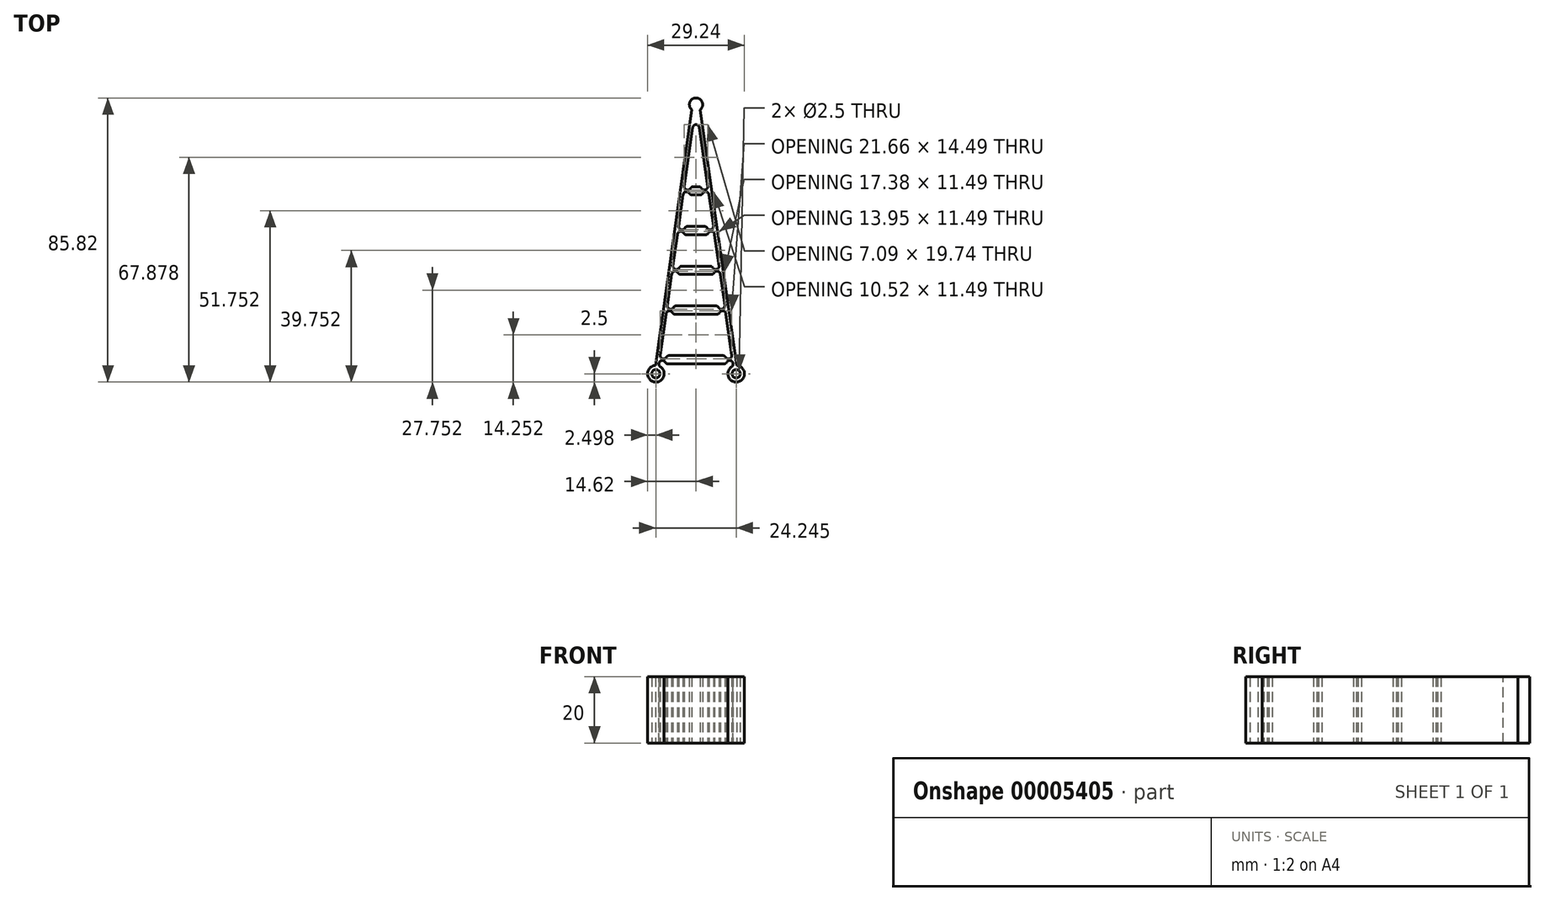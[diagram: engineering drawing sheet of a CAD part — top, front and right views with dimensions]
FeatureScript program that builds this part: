
annotation { "Feature Type Name" : "Feature", "Feature Type Description" : "" }
export const myFeature = defineFeature(function(context is Context, id is Id, definition is map)
    precondition{}
    {
        {
            var Q0;
            Q0=qCreatedBy(makeId("Top.planeOp"),FACE);
            var sketch = newSketch(context, id + "F0", { "sketchPlane" : qUnion([Q0])});
            skLineSegment(sketch, "E0", {"start": v(10, 0) * mm, "end": v(0, 70) * mm});
            skLineSegment(sketch, "E1", {"start": v(0, 70) * mm, "end": v(-10, 0) * mm});
            skLineSegment(sketch, "E2", {"start": v(-10, 0) * mm, "end": v(10, 0) * mm});
            skLineSegment(sketch, "E3", {"start": v(-2.71, 51) * mm, "end": v(2.71, 51) * mm});
            skLineSegment(sketch, "E4", {"start": v(-4.43, 39) * mm, "end": v(4.43, 39) * mm});
            skLineSegment(sketch, "E5", {"start": v(-6.14, 27) * mm, "end": v(6.14, 27) * mm});
            skLineSegment(sketch, "E6", {"start": v(-7.86, 15) * mm, "end": v(7.86, 15) * mm});
            skCircle(sketch, "E7", {"center": v(2.71, 51) * mm, "radius": 1.5 * mm});
            skCircle(sketch, "E8", {"center": v(4.43, 39) * mm, "radius": 1.5 * mm});
            skCircle(sketch, "E9", {"center": v(6.14, 27) * mm, "radius": 1.5 * mm});
            skCircle(sketch, "E10", {"center": v(7.86, 15) * mm, "radius": 1.5 * mm});
            skCircle(sketch, "E11", {"center": v(10, 0) * mm, "radius": 1.5 * mm});
            skSolve(sketch);
        }
        {
            var Q0;
            Q0=qCreatedBy(makeId("Top.planeOp"),FACE);
            var sketch = newSketch(context, id + "F1", { "sketchPlane" : qUnion([Q0])});
            skLineSegment(sketch, "E12", {"start": v(0, 77.07) * mm, "end": v(11.62, -4.25) * mm});
            skLineSegment(sketch, "E13", {"start": v(11.62, -4.25) * mm, "end": v(12.63, -4.25) * mm});
            skLineSegment(sketch, "E14", {"start": v(12.63, -4.25) * mm, "end": v(0.99, 77.21) * mm});
            skLineSegment(sketch, "E15", {"start": v(0.99, 77.21) * mm, "end": v(0, 77.07) * mm});
            skLineSegment(sketch, "E16", {"start": v(0, 77.07) * mm, "end": v(0, 0) * mm, "construction": true});
            skLineSegment(sketch, "E17.bottom", {"start": v(0, 49.75) * mm, "end": v(3.9, 49.75) * mm});
            skLineSegment(sketch, "E17.top", {"start": v(0, 52.25) * mm, "end": v(3.9, 52.25) * mm});
            skLineSegment(sketch, "E17.left", {"start": v(0, 49.75) * mm, "end": v(0, 52.25) * mm});
            skLineSegment(sketch, "E17.right", {"start": v(3.9, 49.75) * mm, "end": v(3.9, 52.25) * mm});
            skLineSegment(sketch, "E18.bottom", {"start": v(0, 40.25) * mm, "end": v(5.62, 40.25) * mm});
            skLineSegment(sketch, "E18.top", {"start": v(0, 37.75) * mm, "end": v(5.62, 37.75) * mm});
            skLineSegment(sketch, "E18.left", {"start": v(0, 40.25) * mm, "end": v(0, 37.75) * mm});
            skLineSegment(sketch, "E18.right", {"start": v(5.62, 40.25) * mm, "end": v(5.62, 37.75) * mm});
            skLineSegment(sketch, "E19.bottom", {"start": v(0, 28.25) * mm, "end": v(7.33, 28.25) * mm});
            skLineSegment(sketch, "E19.top", {"start": v(0, 25.75) * mm, "end": v(7.33, 25.75) * mm});
            skLineSegment(sketch, "E19.left", {"start": v(0, 28.25) * mm, "end": v(0, 25.75) * mm});
            skLineSegment(sketch, "E19.right", {"start": v(7.33, 28.25) * mm, "end": v(7.33, 25.75) * mm});
            skLineSegment(sketch, "E20.bottom", {"start": v(0, 16.25) * mm, "end": v(9.05, 16.25) * mm});
            skLineSegment(sketch, "E20.top", {"start": v(0, 13.75) * mm, "end": v(9.05, 13.75) * mm});
            skLineSegment(sketch, "E20.left", {"start": v(0, 16.25) * mm, "end": v(0, 13.75) * mm});
            skLineSegment(sketch, "E20.right", {"start": v(9.05, 16.25) * mm, "end": v(9.05, 13.75) * mm});
            skLineSegment(sketch, "E21.bottom", {"start": v(0, 1.25) * mm, "end": v(11.19, 1.25) * mm});
            skLineSegment(sketch, "E21.top", {"start": v(0, -1.25) * mm, "end": v(11.19, -1.25) * mm});
            skLineSegment(sketch, "E21.left", {"start": v(0, 1.25) * mm, "end": v(0, -1.25) * mm});
            skLineSegment(sketch, "E21.right", {"start": v(11.19, 1.25) * mm, "end": v(11.19, -1.25) * mm});
            skPoint(sketch, "E22", {"position": v(0, 51) * mm});
            skPoint(sketch, "E23", {"position": v(0, 39) * mm});
            skPoint(sketch, "E24", {"position": v(0, 27) * mm});
            skPoint(sketch, "E25", {"position": v(0, 15) * mm});
            skArc(sketch, "E26", {"start": v(0.28, 75.1) * mm, "mid": v(1.31, 78.58) * mm, "end": v(-2, 77.07) * mm});
            skLineSegment(sketch, "E27", {"start": v(0, 77.07) * mm, "end": v(-2, 77.07) * mm});
            skCircle(sketch, "E28", {"center": v(12.12, -4.25) * mm, "radius": 2.5 * mm});
            skSolve(sketch);
        }
        {
            var Q0;
            Q0=qCreatedBy(makeId("Top.planeOp"),FACE);
            var sketch = newSketch(context, id + "F2", { "sketchPlane" : qUnion([Q0])});
            skCircle(sketch, "E29", {"center": v(2.54, 52.25) * mm, "radius": 1 * mm});
            skCircle(sketch, "E30", {"center": v(2.9, 49.75) * mm, "radius": 1 * mm});
            skCircle(sketch, "E31", {"center": v(4.25, 40.25) * mm, "radius": 1 * mm});
            skCircle(sketch, "E32", {"center": v(4.6, 37.75) * mm, "radius": 1 * mm});
            skCircle(sketch, "E33", {"center": v(5.96, 28.25) * mm, "radius": 1 * mm});
            skCircle(sketch, "E34", {"center": v(6.32, 25.75) * mm, "radius": 1 * mm});
            skCircle(sketch, "E35", {"center": v(7.68, 16.25) * mm, "radius": 1 * mm});
            skCircle(sketch, "E36", {"center": v(8.04, 13.75) * mm, "radius": 1 * mm});
            skCircle(sketch, "E37", {"center": v(9.82, 1.25) * mm, "radius": 1 * mm});
            skCircle(sketch, "E38", {"center": v(10.18, -1.25) * mm, "radius": 1 * mm});
            skSolve(sketch);
        }
        {
            var Q0;
            Q0=qCreatedBy(makeId("Top.planeOp"),FACE);
            var sketch = newSketch(context, id + "F3", { "sketchPlane" : qUnion([Q0])});
            skCircle(sketch, "E39", {"center": v(12.12, -4.25) * mm, "radius": 1.25 * mm});
            skSolve(sketch);
        }
        {
            var Q0;
            {var subQ4=sQuery(id+"F1.wireOp",EDGE,"E17.bottom");var subQ5=sQuery(id+"F1.wireOp",EDGE,"E17.right");var subQ9=sQuery(id+"F1.wireOp",EDGE,"E18.top");var subQ12=sQuery(id+"F1.wireOp",EDGE,"E18.right");var subQ16=sQuery(id+"F1.wireOp",EDGE,"E19.top");var subQ19=sQuery(id+"F1.wireOp",EDGE,"E19.right");var subQ23=sQuery(id+"F1.wireOp",EDGE,"E20.top");var subQ26=sQuery(id+"F1.wireOp",EDGE,"E20.right");var subQ30=sQuery(id+"F1.wireOp",EDGE,"E21.top");var subQ33=sQuery(id+"F1.wireOp",EDGE,"E21.right");var subQ40=sQuery(id+"F1.wireOp",EDGE,"E13");var subQ42=makeQuery(id+"F1.imprint","IMPRINT",EDGE,{"derivedFrom":subQ40});var subQ47=sQuery(id+"F1.wireOp",EDGE,"E15");var subQ48=makeQuery(id+"F1.imprint","IMPRINT",EDGE,{"derivedFrom":subQ47});var subQ52=makeQuery(id+"F1.imprint","IMPRINT",EDGE,{"derivedFrom":subQ5});var subQ54=makeQuery(id+"F1.imprint","IMPRINT",EDGE,{"derivedFrom":subQ12});var subQ56=makeQuery(id+"F1.imprint","IMPRINT",EDGE,{"derivedFrom":subQ19});var subQ58=makeQuery(id+"F1.imprint","IMPRINT",EDGE,{"derivedFrom":subQ26});var subQ60=makeQuery(id+"F1.imprint","IMPRINT",EDGE,{"derivedFrom":subQ33});Q0=qUnion([makeQuery(id+"F1.imprint","IMPRINT",FACE,{"disambiguationData":[TD([[makeQuery(id+"F1.imprint","IMPRINT",EDGE,{"derivedFrom":subQ4}),1.0]])]}),makeQuery(id+"F1.imprint","IMPRINT",FACE,{"disambiguationData":[TD([[makeQuery(id+"F1.imprint","IMPRINT",EDGE,{"derivedFrom":subQ9}),1.0]])]}),makeQuery(id+"F1.imprint","IMPRINT",FACE,{"disambiguationData":[TD([[makeQuery(id+"F1.imprint","IMPRINT",EDGE,{"derivedFrom":subQ16}),1.0]])]}),makeQuery(id+"F1.imprint","IMPRINT",FACE,{"disambiguationData":[TD([[makeQuery(id+"F1.imprint","IMPRINT",EDGE,{"derivedFrom":subQ23}),1.0]])]}),makeQuery(id+"F1.imprint","IMPRINT",FACE,{"disambiguationData":[TD([[makeQuery(id+"F1.imprint","IMPRINT",EDGE,{"derivedFrom":subQ30}),1.0]])]}),makeQuery(id+"F1.imprint","IMPRINT",FACE,{"disambiguationData":[TD([[subQ42,-1.0]])]}),makeQuery(id+"F1.imprint","IMPRINT",FACE,{"disambiguationData":[TD([[subQ48,-1.0]])]}),makeQuery(id+"F1.imprint","IMPRINT",FACE,{"disambiguationData":[TD([[subQ48,1.0]])]}),makeQuery(id+"F1.imprint","IMPRINT",FACE,{"disambiguationData":[TD([[subQ52,1.0]])]}),makeQuery(id+"F1.imprint","IMPRINT",FACE,{"disambiguationData":[TD([[subQ54,-1.0]])]}),makeQuery(id+"F1.imprint","IMPRINT",FACE,{"disambiguationData":[TD([[subQ56,-1.0]])]}),makeQuery(id+"F1.imprint","IMPRINT",FACE,{"disambiguationData":[TD([[subQ58,-1.0]])]}),makeQuery(id+"F1.imprint","IMPRINT",FACE,{"disambiguationData":[TD([[subQ60,-1.0]])]}),makeQuery(id+"F1.imprint","IMPRINT",FACE,{"disambiguationData":[TD([[subQ42,1.0]])]}),makeQuery(id+"F1.imprint","IMPRINT",FACE,{"disambiguationData":[TD([[subQ52,-1.0]])]})]);}
            var Q1;
            {var subQ5=sQuery(id+"F1.wireOp",EDGE,"E13");Q1=makeQuery(id+"F1.imprint","IMPRINT",FACE,{"disambiguationData":[TD([[makeQuery(id+"F1.imprint","IMPRINT",EDGE,{"derivedFrom":subQ5}),1.0]])]});}
            extrude(context, id + "F4", {"entities" : qUnion([Q0, Q1]), "depth" : 20 * mm});
        }
        {
            var Q0;
            {Q0=qUnion([makeQuery(id+"F2.imprint","IMPRINT",FACE,{"disambiguationData":[TD([[makeQuery(id+"F2.imprint","IMPRINT",EDGE,{"derivedFrom":sQuery(id+"F2.wireOp",EDGE,"E29")}),1.0]])]}),makeQuery(id+"F2.imprint","IMPRINT",FACE,{"disambiguationData":[TD([[makeQuery(id+"F2.imprint","IMPRINT",EDGE,{"derivedFrom":sQuery(id+"F2.wireOp",EDGE,"E30")}),1.0]])]}),makeQuery(id+"F2.imprint","IMPRINT",FACE,{"disambiguationData":[TD([[makeQuery(id+"F2.imprint","IMPRINT",EDGE,{"derivedFrom":sQuery(id+"F2.wireOp",EDGE,"E31")}),1.0]])]}),makeQuery(id+"F2.imprint","IMPRINT",FACE,{"disambiguationData":[TD([[makeQuery(id+"F2.imprint","IMPRINT",EDGE,{"derivedFrom":sQuery(id+"F2.wireOp",EDGE,"E32")}),1.0]])]}),makeQuery(id+"F2.imprint","IMPRINT",FACE,{"disambiguationData":[TD([[makeQuery(id+"F2.imprint","IMPRINT",EDGE,{"derivedFrom":sQuery(id+"F2.wireOp",EDGE,"E33")}),1.0]])]}),makeQuery(id+"F2.imprint","IMPRINT",FACE,{"disambiguationData":[TD([[makeQuery(id+"F2.imprint","IMPRINT",EDGE,{"derivedFrom":sQuery(id+"F2.wireOp",EDGE,"E34")}),1.0]])]}),makeQuery(id+"F2.imprint","IMPRINT",FACE,{"disambiguationData":[TD([[makeQuery(id+"F2.imprint","IMPRINT",EDGE,{"derivedFrom":sQuery(id+"F2.wireOp",EDGE,"E35")}),1.0]])]}),makeQuery(id+"F2.imprint","IMPRINT",FACE,{"disambiguationData":[TD([[makeQuery(id+"F2.imprint","IMPRINT",EDGE,{"derivedFrom":sQuery(id+"F2.wireOp",EDGE,"E36")}),1.0]])]}),makeQuery(id+"F2.imprint","IMPRINT",FACE,{"disambiguationData":[TD([[makeQuery(id+"F2.imprint","IMPRINT",EDGE,{"derivedFrom":sQuery(id+"F2.wireOp",EDGE,"E37")}),1.0]])]}),makeQuery(id+"F2.imprint","IMPRINT",FACE,{"disambiguationData":[TD([[makeQuery(id+"F2.imprint","IMPRINT",EDGE,{"derivedFrom":sQuery(id+"F2.wireOp",EDGE,"E38")}),1.0]])]})]);}
            extrude(context, id + "F5", {"entities" : qUnion([Q0]), "operationType" : NewBodyOperationType.REMOVE, "endBound" : BoundingType.THROUGH_ALL, "depth" : 25 * mm});
        }
        {
            var Q0;
            Q0=makeQuery(id+"F3.imprint","IMPRINT",FACE,{"disambiguationData":[TD([[makeQuery(id+"F3.imprint","IMPRINT",EDGE,{"derivedFrom":sQuery(id+"F3.wireOp",EDGE,"E39")}),1.0]])]});
            extrude(context, id + "F6", {"entities" : qUnion([Q0]), "operationType" : NewBodyOperationType.REMOVE, "endBound" : BoundingType.THROUGH_ALL, "depth" : 25 * mm});
        }
        {
            var Q0;
            Q0=makeQuery(id+"F5.boolean.opBoolean","INTERSECT",EDGE,{"disambiguationData":[OD(0.0)],"derivedFrom":[makeQuery(id+"F4.opExtrude","SWEPT_FACE",FACE,{"disambiguationData":[OSD([sQuery(id+"F1.wireOp",EDGE,"E17.top")])]}),makeQuery(id+"F5.opExtrude","SWEPT_FACE",FACE,{"disambiguationData":[OSD([sQuery(id+"F2.wireOp",EDGE,"E29")])]})]});
            var Q1;
            Q1=makeQuery(id+"F5.boolean.opBoolean","INTERSECT",EDGE,{"disambiguationData":[OD(0.0)],"derivedFrom":[makeQuery(id+"F4.opExtrude","SWEPT_FACE",FACE,{"disambiguationData":[OSD([sQuery(id+"F1.wireOp",EDGE,"E17.bottom")])]}),makeQuery(id+"F5.opExtrude","SWEPT_FACE",FACE,{"disambiguationData":[OSD([sQuery(id+"F2.wireOp",EDGE,"E30")])]})]});
            var Q2;
            Q2=makeQuery(id+"F5.boolean.opBoolean","INTERSECT",EDGE,{"disambiguationData":[OD(0.0)],"derivedFrom":[makeQuery(id+"F4.opExtrude","SWEPT_FACE",FACE,{"disambiguationData":[OSD([sQuery(id+"F1.wireOp",EDGE,"E18.bottom")])]}),makeQuery(id+"F5.opExtrude","SWEPT_FACE",FACE,{"disambiguationData":[OSD([sQuery(id+"F2.wireOp",EDGE,"E31")])]})]});
            var Q3;
            Q3=makeQuery(id+"F5.boolean.opBoolean","INTERSECT",EDGE,{"disambiguationData":[OD(0.0)],"derivedFrom":[makeQuery(id+"F4.opExtrude","SWEPT_FACE",FACE,{"disambiguationData":[OSD([sQuery(id+"F1.wireOp",EDGE,"E18.top")])]}),makeQuery(id+"F5.opExtrude","SWEPT_FACE",FACE,{"disambiguationData":[OSD([sQuery(id+"F2.wireOp",EDGE,"E32")])]})]});
            var Q4;
            Q4=makeQuery(id+"F5.boolean.opBoolean","INTERSECT",EDGE,{"disambiguationData":[OD(0.0)],"derivedFrom":[makeQuery(id+"F4.opExtrude","SWEPT_FACE",FACE,{"disambiguationData":[OSD([sQuery(id+"F1.wireOp",EDGE,"E19.top")])]}),makeQuery(id+"F5.opExtrude","SWEPT_FACE",FACE,{"disambiguationData":[OSD([sQuery(id+"F2.wireOp",EDGE,"E34")])]})]});
            var Q5;
            Q5=makeQuery(id+"F5.boolean.opBoolean","INTERSECT",EDGE,{"disambiguationData":[OD(0.0)],"derivedFrom":[makeQuery(id+"F4.opExtrude","SWEPT_FACE",FACE,{"disambiguationData":[OSD([sQuery(id+"F1.wireOp",EDGE,"E19.bottom")])]}),makeQuery(id+"F5.opExtrude","SWEPT_FACE",FACE,{"disambiguationData":[OSD([sQuery(id+"F2.wireOp",EDGE,"E33")])]})]});
            var Q6;
            Q6=makeQuery(id+"F5.boolean.opBoolean","INTERSECT",EDGE,{"disambiguationData":[OD(0.0)],"derivedFrom":[makeQuery(id+"F4.opExtrude","SWEPT_FACE",FACE,{"disambiguationData":[OSD([sQuery(id+"F1.wireOp",EDGE,"E20.bottom")])]}),makeQuery(id+"F5.opExtrude","SWEPT_FACE",FACE,{"disambiguationData":[OSD([sQuery(id+"F2.wireOp",EDGE,"E35")])]})]});
            var Q7;
            Q7=makeQuery(id+"F5.boolean.opBoolean","INTERSECT",EDGE,{"disambiguationData":[OD(0.0)],"derivedFrom":[makeQuery(id+"F4.opExtrude","SWEPT_FACE",FACE,{"disambiguationData":[OSD([sQuery(id+"F1.wireOp",EDGE,"E20.top")])]}),makeQuery(id+"F5.opExtrude","SWEPT_FACE",FACE,{"disambiguationData":[OSD([sQuery(id+"F2.wireOp",EDGE,"E36")])]})]});
            var Q8;
            Q8=makeQuery(id+"F5.boolean.opBoolean","INTERSECT",EDGE,{"disambiguationData":[OD(0.0)],"derivedFrom":[makeQuery(id+"F4.opExtrude","SWEPT_FACE",FACE,{"disambiguationData":[OSD([sQuery(id+"F1.wireOp",EDGE,"E21.bottom")])]}),makeQuery(id+"F5.opExtrude","SWEPT_FACE",FACE,{"disambiguationData":[OSD([sQuery(id+"F2.wireOp",EDGE,"E37")])]})]});
            var Q9;
            Q9=makeQuery(id+"F5.boolean.opBoolean","INTERSECT",EDGE,{"disambiguationData":[OD(0.0)],"derivedFrom":[makeQuery(id+"F4.opExtrude","SWEPT_FACE",FACE,{"disambiguationData":[OSD([sQuery(id+"F1.wireOp",EDGE,"E21.top")])]}),makeQuery(id+"F5.opExtrude","SWEPT_FACE",FACE,{"disambiguationData":[OSD([sQuery(id+"F2.wireOp",EDGE,"E38")])]})]});
            var Q10;
            Q10=makeQuery(id+"F4.opExtrude","SWEPT_EDGE",EDGE,{"disambiguationData":[OSD([sQuery(id+"F1.wireOp",EDGE,"E12"),sQuery(id+"F1.wireOp",EDGE,"E28")])]});
            fillet(context, id + "F7", {"entities" : qUnion([Q0, Q1, Q2, Q3, Q4, Q5, Q6, Q7, Q8, Q9, Q10]), "radius" : 1 * mm, "tangentPropagation" : true, "allowEdgeOverflow" : false});
        }
        {
            var Q0;
            Q0=makeQuery(id+"F4.opExtrude","SWEPT_BODY",BODY,{"disambiguationData":[OSD([sQuery(id+"F1.wireOp",EDGE,"E12"),sQuery(id+"F1.wireOp",EDGE,"E14"),sQuery(id+"F1.wireOp",EDGE,"E17.bottom"),sQuery(id+"F1.wireOp",EDGE,"E17.top"),sQuery(id+"F1.wireOp",EDGE,"E17.left"),sQuery(id+"F1.wireOp",EDGE,"E18.bottom"),sQuery(id+"F1.wireOp",EDGE,"E18.top"),sQuery(id+"F1.wireOp",EDGE,"E18.left"),sQuery(id+"F1.wireOp",EDGE,"E19.bottom"),sQuery(id+"F1.wireOp",EDGE,"E19.top"),sQuery(id+"F1.wireOp",EDGE,"E19.left"),sQuery(id+"F1.wireOp",EDGE,"E20.bottom"),sQuery(id+"F1.wireOp",EDGE,"E20.top"),sQuery(id+"F1.wireOp",EDGE,"E20.left"),sQuery(id+"F1.wireOp",EDGE,"E21.bottom"),sQuery(id+"F1.wireOp",EDGE,"E21.top"),sQuery(id+"F1.wireOp",EDGE,"E21.left"),sQuery(id+"F1.wireOp",EDGE,"E26"),sQuery(id+"F1.wireOp",EDGE,"E27"),sQuery(id+"F1.wireOp",EDGE,"E28")])]});
            var Q1;
            Q1=qCreatedBy(makeId("Right.planeOp"),FACE);
            mirror(context, id + "F8", {"entities" : qUnion([Q0]), "mirrorPlane" : qUnion([Q1])});
        }
        {
            var Q0;
            Q0=makeQuery(id+"F4.opExtrude","SWEPT_BODY",BODY,{"disambiguationData":[OSD([sQuery(id+"F1.wireOp",EDGE,"E12"),sQuery(id+"F1.wireOp",EDGE,"E14"),sQuery(id+"F1.wireOp",EDGE,"E17.bottom"),sQuery(id+"F1.wireOp",EDGE,"E17.top"),sQuery(id+"F1.wireOp",EDGE,"E17.left"),sQuery(id+"F1.wireOp",EDGE,"E18.bottom"),sQuery(id+"F1.wireOp",EDGE,"E18.top"),sQuery(id+"F1.wireOp",EDGE,"E18.left"),sQuery(id+"F1.wireOp",EDGE,"E19.bottom"),sQuery(id+"F1.wireOp",EDGE,"E19.top"),sQuery(id+"F1.wireOp",EDGE,"E19.left"),sQuery(id+"F1.wireOp",EDGE,"E20.bottom"),sQuery(id+"F1.wireOp",EDGE,"E20.top"),sQuery(id+"F1.wireOp",EDGE,"E20.left"),sQuery(id+"F1.wireOp",EDGE,"E21.bottom"),sQuery(id+"F1.wireOp",EDGE,"E21.top"),sQuery(id+"F1.wireOp",EDGE,"E21.left"),sQuery(id+"F1.wireOp",EDGE,"E26"),sQuery(id+"F1.wireOp",EDGE,"E27"),sQuery(id+"F1.wireOp",EDGE,"E28")])]});
            var Q1;
            Q1=makeQuery(id+"F8.opPattern","COPY",BODY,{"derivedFrom":makeQuery(id+"F4.opExtrude","SWEPT_BODY",BODY,{"disambiguationData":[OSD([sQuery(id+"F1.wireOp",EDGE,"E12"),sQuery(id+"F1.wireOp",EDGE,"E14"),sQuery(id+"F1.wireOp",EDGE,"E17.bottom"),sQuery(id+"F1.wireOp",EDGE,"E17.top"),sQuery(id+"F1.wireOp",EDGE,"E17.left"),sQuery(id+"F1.wireOp",EDGE,"E18.bottom"),sQuery(id+"F1.wireOp",EDGE,"E18.top"),sQuery(id+"F1.wireOp",EDGE,"E18.left"),sQuery(id+"F1.wireOp",EDGE,"E19.bottom"),sQuery(id+"F1.wireOp",EDGE,"E19.top"),sQuery(id+"F1.wireOp",EDGE,"E19.left"),sQuery(id+"F1.wireOp",EDGE,"E20.bottom"),sQuery(id+"F1.wireOp",EDGE,"E20.top"),sQuery(id+"F1.wireOp",EDGE,"E20.left"),sQuery(id+"F1.wireOp",EDGE,"E21.bottom"),sQuery(id+"F1.wireOp",EDGE,"E21.top"),sQuery(id+"F1.wireOp",EDGE,"E21.left"),sQuery(id+"F1.wireOp",EDGE,"E26"),sQuery(id+"F1.wireOp",EDGE,"E27"),sQuery(id+"F1.wireOp",EDGE,"E28")])]}),"instanceName":"1"});
            booleanBodies(context, id + "F9", {"operationType" : BooleanOperationType.UNION, "tools" : qUnion([Q0, Q1])});
        }
        {
            var Q0;
            {var subQ0=makeQuery(id+"F4.opExtrude","SWEPT_EDGE",EDGE,{"disambiguationData":[OSD([sQuery(id+"F1.wireOp",EDGE,"E12"),sQuery(id+"F1.wireOp",EDGE,"E15"),sQuery(id+"F1.wireOp",EDGE,"E27")])]});Q0=makeQuery(id+"F9.opBoolean","MERGE",EDGE,{"derivedFrom":[subQ0,makeQuery(id+"F8.opPattern","COPY",EDGE,{"derivedFrom":subQ0,"instanceName":"1"})]});}
            fillet(context, id + "F10", {"entities" : qUnion([Q0]), "radius" : 1 * mm, "tangentPropagation" : true, "allowEdgeOverflow" : false});
        }
    });
